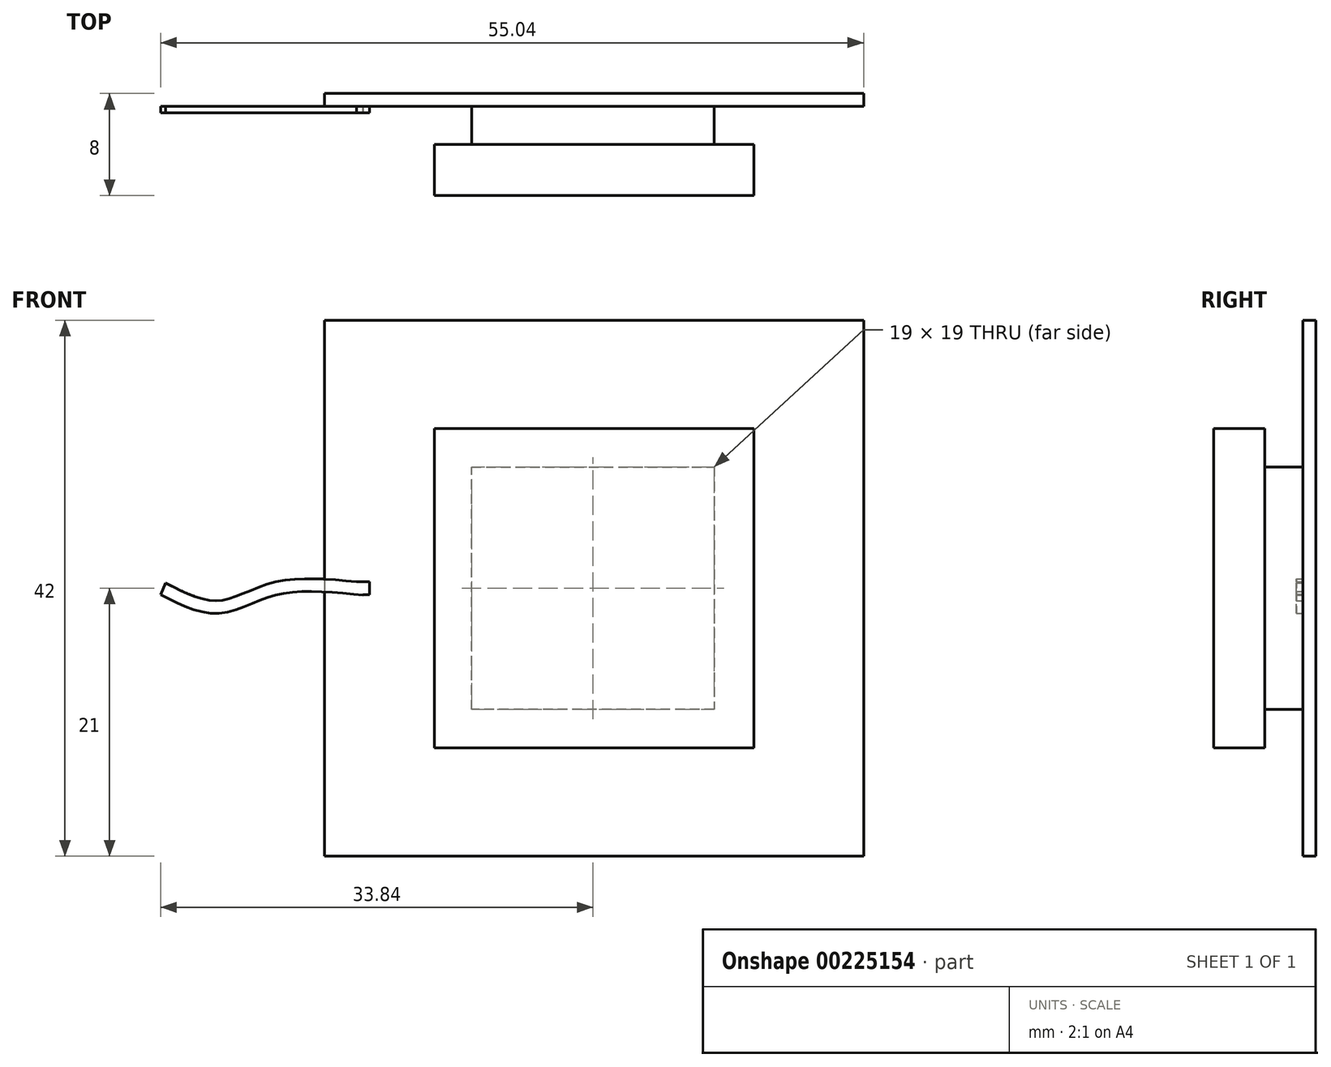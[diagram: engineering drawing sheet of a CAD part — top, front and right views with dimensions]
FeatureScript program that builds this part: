
annotation { "Feature Type Name" : "Feature", "Feature Type Description" : "" }
export const myFeature = defineFeature(function(context is Context, id is Id, definition is map)
    precondition{}
    {
        {
            var Q0;
            Q0=qCreatedBy(makeId("Front.planeOp"),FACE);
            var sketch = newSketch(context, id + "F0", { "sketchPlane" : qUnion([Q0])});
            skLineSegment(sketch, "E0", {"start": v(-21.1, -21) * mm, "end": v(21.1, -21) * mm});
            skLineSegment(sketch, "E1", {"start": v(21.1, -21) * mm, "end": v(21.1, 21) * mm});
            skLineSegment(sketch, "E2", {"start": v(21.1, 21) * mm, "end": v(-21.1, 21) * mm});
            skLineSegment(sketch, "E3", {"start": v(-21.1, 21) * mm, "end": v(-21.1, -21) * mm});
            skLineSegment(sketch, "E4", {"start": v(-21.1, -21) * mm, "end": v(-12.6, -21) * mm, "construction": true});
            skLineSegment(sketch, "E5", {"start": v(-12.6, -21) * mm, "end": v(-12.6, -12.5) * mm, "construction": true});
            skLineSegment(sketch, "E6", {"start": v(-12.6, -9.5) * mm, "end": v(-9.6, -9.5) * mm, "construction": true});
            skLineSegment(sketch, "E7", {"start": v(2.29, -17.68) * mm, "end": v(2.29, -14.68) * mm, "construction": true});
            skLineSegment(sketch, "E8", {"start": v(-12.6, 12.5) * mm, "end": v(-12.6, 9.5) * mm, "construction": true});
            skLineSegment(sketch, "E9", {"start": v(-12.6, 9.5) * mm, "end": v(-9.6, 9.5) * mm, "construction": true});
            skLineSegment(sketch, "E10", {"start": v(2.29, 7.32) * mm, "end": v(2.29, 4.32) * mm, "construction": true});
            skLineSegment(sketch, "E11", {"start": v(-9.6, 9.5) * mm, "end": v(-9.6, -9.5) * mm});
            skLineSegment(sketch, "E12", {"start": v(-9.6, -9.5) * mm, "end": v(9.4, -9.5) * mm});
            skLineSegment(sketch, "E13", {"start": v(9.4, -9.5) * mm, "end": v(9.4, 9.5) * mm});
            skLineSegment(sketch, "E14", {"start": v(9.4, 9.5) * mm, "end": v(-9.6, 9.5) * mm});
            skLineSegment(sketch, "E15", {"start": v(-9.6, -9.5) * mm, "end": v(-12.6, -9.5) * mm});
            skLineSegment(sketch, "E16", {"start": v(-12.6, -12.5) * mm, "end": v(-12.6, -9.5) * mm});
            skLineSegment(sketch, "E17", {"start": v(9.4, 9.5) * mm, "end": v(13.07, 9.5) * mm});
            skLineSegment(sketch, "E18", {"start": v(13.07, 9.5) * mm, "end": v(-9.6, 9.5) * mm});
            skLineSegment(sketch, "E19", {"start": v(21.1, 21) * mm, "end": v(-21.1, -21) * mm, "construction": true});
            skLineSegment(sketch, "E20", {"start": v(21.1, -21) * mm, "end": v(-21.1, 21) * mm, "construction": true});
            skPoint(sketch, "E21", {"position": v(0, 0) * mm});
            skLineSegment(sketch, "E22", {"start": v(-21.1, 21) * mm, "end": v(-24.1, 21) * mm, "construction": true});
            skLineSegment(sketch, "E23", {"start": v(-24.1, 21) * mm, "end": v(-24.1, 0) * mm, "construction": true});
            skLineSegment(sketch, "E24", {"start": v(-21.1, -21) * mm, "end": v(-24.1, -21) * mm, "construction": true});
            skLineSegment(sketch, "E25", {"start": v(-24.1, -21) * mm, "end": v(-24.1, 0) * mm, "construction": true});
            skLineSegment(sketch, "E26", {"start": v(-24.1, 0) * mm, "end": v(-18.1, 0) * mm, "construction": true});
            skPoint(sketch, "E26.endSnap0", {"position": v(-21.1, 0) * mm});
            skLineSegment(sketch, "E27.bottom", {"start": v(-18.6, -0.5) * mm, "end": v(-17.6, -0.5) * mm});
            skLineSegment(sketch, "E27.top", {"start": v(-18.6, 0.5) * mm, "end": v(-17.6, 0.5) * mm});
            skLineSegment(sketch, "E27.left", {"start": v(-18.6, -0.5) * mm, "end": v(-18.6, 0.5) * mm});
            skLineSegment(sketch, "E27.right", {"start": v(-17.6, -0.5) * mm, "end": v(-17.6, 0.5) * mm});
            skPoint(sketch, "E27.middle", {"position": v(-18.1, 0) * mm});
            skFitSpline(sketch, "E28", {"points": [v(-18.1, 0) * mm, v(-25.07, 0) * mm, v(-29.4, -1.42) * mm, v(-33.73, 0) * mm], "startDerivative": vector(-19.39, 2) * mm, "endDerivative": vector(-14, 7.31) * mm});
            skSolve(sketch);
        }
        {
            var Q0;
            Q0=makeQuery(id+"F0.imprint","IMPRINT",FACE,{"disambiguationData":[TD([[makeQuery(id+"F0.imprint","IMPRINT",EDGE,{"derivedFrom":sQuery(id+"F0.wireOp",EDGE,"E0")}),1.0]])]});
            var Q1;
            Q1=makeQuery(id+"F0.imprint","IMPRINT",FACE,{"disambiguationData":[TD([[makeQuery(id+"F0.imprint","IMPRINT",EDGE,{"derivedFrom":sQuery(id+"F0.wireOp",EDGE,"oFwmUpxB-NSXD-AdKg-Rr5l-mAlETXPV7E1B")}),1.0]])]});
            var Q2;
            Q2=makeQuery(id+"F0.imprint","IMPRINT",FACE,{"disambiguationData":[TD([[makeQuery(id+"F0.imprint","IMPRINT",EDGE,{"derivedFrom":sQuery(id+"F0.wireOp",EDGE,"E11")}),1.0]])]});
            extrude(context, id + "F1", {"entities" : qUnion([Q0, Q1, Q2]), "depth" : 1 * mm});
        }
        {
            var Q0;
            Q0=makeQuery(id+"F0.imprint","IMPRINT",FACE,{"disambiguationData":[TD([[makeQuery(id+"F0.imprint","IMPRINT",EDGE,{"derivedFrom":sQuery(id+"F0.wireOp",EDGE,"E11")}),1.0]])]});
            extrude(context, id + "F2", {"entities" : qUnion([Q0]), "operationType" : NewBodyOperationType.ADD, "depth" : 4 * mm});
        }
        {
            var Q0;
            Q0=qCreatedBy(makeId("Right.planeOp"),FACE);
            var sketch = newSketch(context, id + "F3", { "sketchPlane" : qUnion([Q0])});
            skLineSegment(sketch, "E29", {"start": v(0, 0) * mm, "end": v(-4, 0) * mm, "construction": true});
            skLineSegment(sketch, "E30", {"start": v(-4, 0) * mm, "end": v(-4, -12.5) * mm, "construction": true});
            skLineSegment(sketch, "E31", {"start": v(-4, 0) * mm, "end": v(-4, 12.5) * mm, "construction": true});
            skLineSegment(sketch, "E32", {"start": v(-4, -12.5) * mm, "end": v(-8, -12.5) * mm});
            skLineSegment(sketch, "E33", {"start": v(-8, -12.5) * mm, "end": v(-8, 12.5) * mm});
            skLineSegment(sketch, "E34", {"start": v(-8, 12.5) * mm, "end": v(-4, 12.5) * mm});
            skLineSegment(sketch, "E35", {"start": v(-4, 12.5) * mm, "end": v(-4, -12.5) * mm});
            skSolve(sketch);
        }
        {
            var Q0;
            Q0=makeQuery(id+"F3.imprint","IMPRINT",FACE,{"disambiguationData":[TD([[makeQuery(id+"F3.imprint","IMPRINT",EDGE,{"derivedFrom":sQuery(id+"F3.wireOp",EDGE,"E32")}),-1.0]])]});
            extrude(context, id + "F4", {"entities" : qUnion([Q0]), "operationType" : NewBodyOperationType.ADD, "depth" : 12.5 * mm});
        }
        {
            var Q0;
            Q0 = qSketchRegion(id + "F3", true);
            extrude(context, id + "F5", {"entities" : qUnion([Q0]), "operationType" : NewBodyOperationType.ADD, "oppositeDirection" : true, "depth" : 12.5 * mm});
        }
        {
            var Q0;
            Q0=makeQuery(id+"F0.imprint","IMPRINT",FACE,{"disambiguationData":[TD([[makeQuery(id+"F0.imprint","IMPRINT",EDGE,{"derivedFrom":sQuery(id+"F0.wireOp",EDGE,"E27.bottom")}),1.0]])]});
            extrude(context, id + "F6", {"entities" : qUnion([Q0]), "operationType" : NewBodyOperationType.ADD, "depth" : 1.5 * mm});
        }
        {
            var Q0;
            Q0=makeQuery(id+"F6.opExtrude","SWEPT_FACE",FACE,{"disambiguationData":[OSD([sQuery(id+"F0.wireOp",EDGE,"E27.left")])]});
            var Q1;
            Q1=sQuery(id+"F0.wireOp",EDGE,"E28");
            sweep(context, id + "F7", {"operationType" : NewBodyOperationType.ADD, "profiles" : qUnion([Q0]), "path" : qUnion([Q1])});
        }
    });
